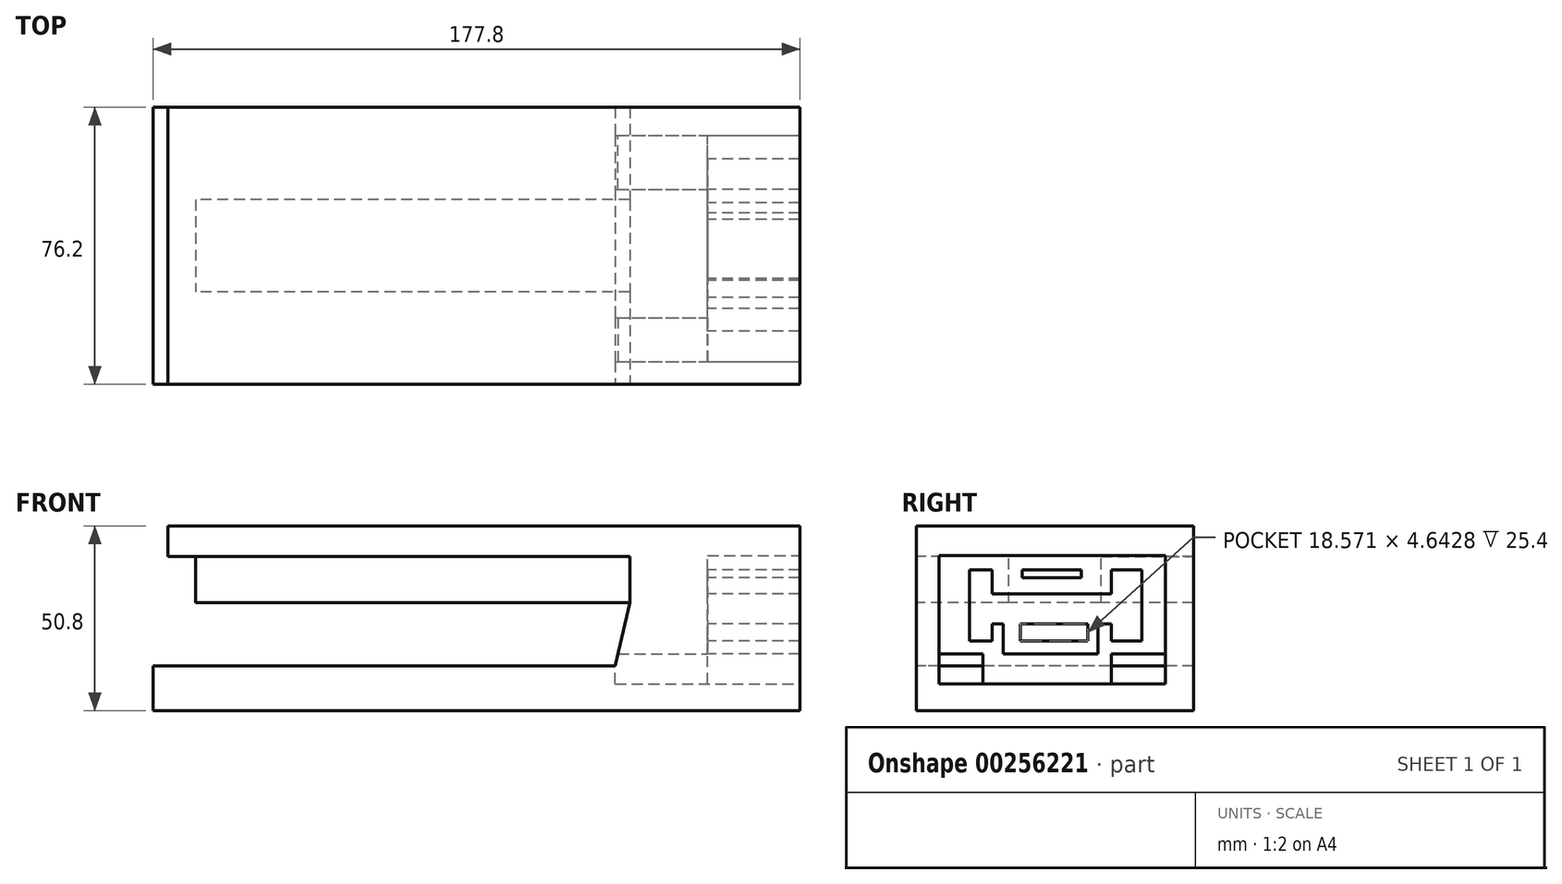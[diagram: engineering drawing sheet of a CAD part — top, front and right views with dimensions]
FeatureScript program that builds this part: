
annotation { "Feature Type Name" : "Feature", "Feature Type Description" : "" }
export const myFeature = defineFeature(function(context is Context, id is Id, definition is map)
    precondition{}
    {
        {
            var Q0;
            Q0=qCreatedBy(makeId("Front.planeOp"),FACE);
            var sketch = newSketch(context, id + "F0", { "sketchPlane" : qUnion([Q0])});
            skLineSegment(sketch, "E0", {"start": v(-114.83, -15.63) * mm, "end": v(62.97, -15.63) * mm});
            skLineSegment(sketch, "E1", {"start": v(62.97, -15.63) * mm, "end": v(62.97, 35.17) * mm});
            skLineSegment(sketch, "E2", {"start": v(62.97, 35.17) * mm, "end": v(-114.83, 35.17) * mm});
            skLineSegment(sketch, "E3", {"start": v(-114.83, 35.17) * mm, "end": v(-114.83, -15.63) * mm});
            skSolve(sketch);
        }
        {
            var Q0;
            Q0=makeQuery(id+"F0.imprint","IMPRINT",FACE,{"disambiguationData":[TD([[makeQuery(id+"F0.imprint","IMPRINT",EDGE,{"derivedFrom":sQuery(id+"F0.wireOp",EDGE,"E0")}),1.0]])]});
            extrude(context, id + "F1", {"entities" : qUnion([Q0]), "depth" : 76.2 * mm});
        }
        {
            var Q0;
            Q0=makeQuery(id+"F1.opExtrude","CAP_FACE",FACE,{"disambiguationData":[OSD([sQuery(id+"F0.wireOp",EDGE,"E0"),sQuery(id+"F0.wireOp",EDGE,"E1"),sQuery(id+"F0.wireOp",EDGE,"E2"),sQuery(id+"F0.wireOp",EDGE,"E3")])],"isStart":false});
            var sketch = newSketch(context, id + "F2", { "sketchPlane" : qUnion([Q0])});
            skLineSegment(sketch, "E4", {"start": v(-114.83, -3.25) * mm, "end": v(12.17, -3.25) * mm});
            skLineSegment(sketch, "E5", {"start": v(12.17, -3.25) * mm, "end": v(16.2, 14.07) * mm});
            skLineSegment(sketch, "E6", {"start": v(16.2, 14.07) * mm, "end": v(-103.19, 14.07) * mm});
            skLineSegment(sketch, "E7", {"start": v(-103.19, 14.07) * mm, "end": v(-103.19, 26.77) * mm});
            skLineSegment(sketch, "E8", {"start": v(-103.19, 26.77) * mm, "end": v(-110.8, 26.77) * mm});
            skLineSegment(sketch, "E9", {"start": v(-110.8, 26.77) * mm, "end": v(-110.8, 35.17) * mm});
            skLineSegment(sketch, "E10", {"start": v(-110.8, 35.17) * mm, "end": v(-114.83, 35.17) * mm});
            skLineSegment(sketch, "E11", {"start": v(-114.83, 35.17) * mm, "end": v(-114.83, -3.25) * mm});
            skSolve(sketch);
        }
        {
            var Q0;
            Q0=makeQuery(id+"F2.imprint","IMPRINT",FACE,{"disambiguationData":[TD([[makeQuery(id+"F2.imprint","IMPRINT",EDGE,{"derivedFrom":sQuery(id+"F2.wireOp",EDGE,"E4")}),1.0]])]});
            extrude(context, id + "F3", {"entities" : qUnion([Q0]), "operationType" : NewBodyOperationType.REMOVE, "oppositeDirection" : true, "depth" : 76.2 * mm});
        }
        {
            var Q0;
            Q0=makeQuery(id+"F1.opExtrude","CAP_FACE",FACE,{"disambiguationData":[OSD([sQuery(id+"F0.wireOp",EDGE,"E0"),sQuery(id+"F0.wireOp",EDGE,"E1"),sQuery(id+"F0.wireOp",EDGE,"E2"),sQuery(id+"F0.wireOp",EDGE,"E3")])],"isStart":false});
            var sketch = newSketch(context, id + "F4", { "sketchPlane" : qUnion([Q0])});
            skLineSegment(sketch, "E12", {"start": v(-103.19, 26.77) * mm, "end": v(16.2, 26.77) * mm});
            skLineSegment(sketch, "E13", {"start": v(16.2, 26.77) * mm, "end": v(16.2, 14.07) * mm});
            skLineSegment(sketch, "E14", {"start": v(16.2, 14.07) * mm, "end": v(-103.19, 14.07) * mm});
            skLineSegment(sketch, "E15", {"start": v(-103.19, 14.07) * mm, "end": v(-103.19, 26.77) * mm});
            skSolve(sketch);
        }
        {
            var Q0;
            Q0=makeQuery(id+"F4.imprint","IMPRINT",FACE,{"disambiguationData":[TD([[makeQuery(id+"F4.imprint","IMPRINT",EDGE,{"derivedFrom":sQuery(id+"F4.wireOp",EDGE,"E12")}),-1.0]])]});
            extrude(context, id + "F5", {"entities" : qUnion([Q0]), "operationType" : NewBodyOperationType.REMOVE, "oppositeDirection" : true, "depth" : 25.4 * mm});
        }
        {
            var Q0;
            Q0=makeQuery(id+"F1.opExtrude","CAP_FACE",FACE,{"disambiguationData":[OSD([sQuery(id+"F0.wireOp",EDGE,"E0"),sQuery(id+"F0.wireOp",EDGE,"E1"),sQuery(id+"F0.wireOp",EDGE,"E2"),sQuery(id+"F0.wireOp",EDGE,"E3")])],"isStart":true});
            var sketch = newSketch(context, id + "F6", { "sketchPlane" : qUnion([Q0])});
            skLineSegment(sketch, "E16", {"start": v(103.19, 26.77) * mm, "end": v(-16.2, 26.77) * mm});
            skLineSegment(sketch, "E17", {"start": v(-16.2, 26.77) * mm, "end": v(-16.2, 14.07) * mm});
            skLineSegment(sketch, "E18", {"start": v(-16.2, 14.07) * mm, "end": v(103.19, 14.07) * mm});
            skLineSegment(sketch, "E19", {"start": v(103.19, 14.07) * mm, "end": v(103.19, 26.77) * mm});
            skSolve(sketch);
        }
        {
            var Q0;
            Q0=makeQuery(id+"F6.imprint","IMPRINT",FACE,{"disambiguationData":[TD([[makeQuery(id+"F6.imprint","IMPRINT",EDGE,{"derivedFrom":sQuery(id+"F6.wireOp",EDGE,"E16")}),1.0]])]});
            extrude(context, id + "F7", {"entities" : qUnion([Q0]), "operationType" : NewBodyOperationType.REMOVE, "oppositeDirection" : true, "depth" : 25.4 * mm});
        }
        {
            var Q0;
            Q0=makeQuery(id+"F1.opExtrude","SWEPT_FACE",FACE,{"disambiguationData":[OSD([sQuery(id+"F0.wireOp",EDGE,"E1")])]});
            var sketch = newSketch(context, id + "F8", { "sketchPlane" : qUnion([Q0])});
            skLineSegment(sketch, "E20.bottom", {"start": v(-69.95, -8.2) * mm, "end": v(-7.74, -8.2) * mm});
            skLineSegment(sketch, "E20.top", {"start": v(-69.95, 27.08) * mm, "end": v(-7.74, 27.08) * mm});
            skLineSegment(sketch, "E20.left", {"start": v(-69.95, -8.2) * mm, "end": v(-69.95, 27.08) * mm});
            skLineSegment(sketch, "E20.right", {"start": v(-7.74, -8.2) * mm, "end": v(-7.74, 27.08) * mm});
            skSolve(sketch);
        }
        {
            var Q0;
            Q0=makeQuery(id+"F8.imprint","IMPRINT",FACE,{"disambiguationData":[TD([[makeQuery(id+"F8.imprint","IMPRINT",EDGE,{"derivedFrom":sQuery(id+"F8.wireOp",EDGE,"E20.bottom")}),1.0]])]});
            extrude(context, id + "F9", {"entities" : qUnion([Q0]), "operationType" : NewBodyOperationType.REMOVE, "oppositeDirection" : true, "depth" : 25.4 * mm});
        }
        {
            var Q0;
            Q0=makeQuery(id+"F9.boolean.opBoolean","COPY",FACE,{"derivedFrom":makeQuery(id+"F9.opExtrude","CAP_FACE",FACE,{"disambiguationData":[OSD([sQuery(id+"F8.wireOp",EDGE,"E20.bottom"),sQuery(id+"F8.wireOp",EDGE,"E20.top"),sQuery(id+"F8.wireOp",EDGE,"E20.left"),sQuery(id+"F8.wireOp",EDGE,"E20.right")])],"isStart":false})});
            var sketch = newSketch(context, id + "F10", { "sketchPlane" : qUnion([Q0])});
            skLineSegment(sketch, "E21", {"start": v(-57.88, -8.2) * mm, "end": v(-57.88, 0) * mm});
            skLineSegment(sketch, "E22", {"start": v(-22.6, -8.2) * mm, "end": v(-22.6, 0) * mm});
            skLineSegment(sketch, "E23", {"start": v(-22.6, 0) * mm, "end": v(-7.74, 0) * mm});
            skLineSegment(sketch, "E24", {"start": v(-7.74, 0) * mm, "end": v(-7.74, -8.2) * mm});
            skLineSegment(sketch, "E25", {"start": v(-7.74, -8.2) * mm, "end": v(-22.6, -8.2) * mm});
            skLineSegment(sketch, "E26", {"start": v(-57.88, -8.2) * mm, "end": v(-69.95, -8.2) * mm});
            skLineSegment(sketch, "E27", {"start": v(-57.88, 0) * mm, "end": v(-69.95, 0) * mm});
            skLineSegment(sketch, "E28", {"start": v(-69.95, 0) * mm, "end": v(-69.95, -8.2) * mm});
            skSolve(sketch);
        }
        {
            var Q0;
            Q0=makeQuery(id+"F10.imprint","IMPRINT",FACE,{"disambiguationData":[TD([[makeQuery(id+"F10.imprint","IMPRINT",EDGE,{"derivedFrom":sQuery(id+"F10.wireOp",EDGE,"E21")}),1.0]])]});
            var Q1;
            Q1=makeQuery(id+"F10.imprint","IMPRINT",FACE,{"disambiguationData":[TD([[makeQuery(id+"F10.imprint","IMPRINT",EDGE,{"derivedFrom":sQuery(id+"F10.wireOp",EDGE,"E22")}),-1.0]])]});
            extrude(context, id + "F11", {"entities" : qUnion([Q0, Q1]), "operationType" : NewBodyOperationType.REMOVE, "oppositeDirection" : true, "depth" : 25.4 * mm});
        }
        {
            var Q0;
            Q0=makeQuery(id+"F9.boolean.opBoolean","COPY",FACE,{"derivedFrom":makeQuery(id+"F9.opExtrude","CAP_FACE",FACE,{"disambiguationData":[OSD([sQuery(id+"F8.wireOp",EDGE,"E20.bottom"),sQuery(id+"F8.wireOp",EDGE,"E20.top"),sQuery(id+"F8.wireOp",EDGE,"E20.left"),sQuery(id+"F8.wireOp",EDGE,"E20.right")])],"isStart":false})});
            var sketch = newSketch(context, id + "F12", { "sketchPlane" : qUnion([Q0])});
            skLineSegment(sketch, "E29", {"start": v(-61.6, 23.06) * mm, "end": v(-61.6, 3.56) * mm});
            skLineSegment(sketch, "E30", {"start": v(-61.6, 3.56) * mm, "end": v(-55.4, 3.56) * mm});
            skLineSegment(sketch, "E31", {"start": v(-55.4, 3.56) * mm, "end": v(-55.4, 8.2) * mm});
            skLineSegment(sketch, "E32", {"start": v(-55.4, 8.2) * mm, "end": v(-52.3, 8.2) * mm});
            skLineSegment(sketch, "E33", {"start": v(-52.3, 8.2) * mm, "end": v(-52.3, 16.56) * mm});
            skLineSegment(sketch, "E34", {"start": v(-52.3, 16.56) * mm, "end": v(-55.4, 16.56) * mm});
            skLineSegment(sketch, "E35", {"start": v(-55.4, 16.56) * mm, "end": v(-55.4, 23.06) * mm});
            skLineSegment(sketch, "E36", {"start": v(-55.4, 23.06) * mm, "end": v(-61.6, 23.06) * mm});
            skLineSegment(sketch, "E37", {"start": v(-14.24, 23.06) * mm, "end": v(-22.6, 23.06) * mm});
            skLineSegment(sketch, "E38", {"start": v(-22.6, 23.06) * mm, "end": v(-22.6, 16.56) * mm});
            skLineSegment(sketch, "E39", {"start": v(-22.6, 16.56) * mm, "end": v(-26.3, 16.56) * mm});
            skLineSegment(sketch, "E40", {"start": v(-26.3, 16.56) * mm, "end": v(-26.3, 8.2) * mm});
            skLineSegment(sketch, "E41", {"start": v(-26.3, 8.2) * mm, "end": v(-22.6, 8.2) * mm});
            skLineSegment(sketch, "E42", {"start": v(-22.6, 8.2) * mm, "end": v(-22.6, 3.56) * mm});
            skLineSegment(sketch, "E43", {"start": v(-22.6, 3.56) * mm, "end": v(-14.24, 3.56) * mm});
            skLineSegment(sketch, "E44", {"start": v(-14.24, 3.56) * mm, "end": v(-14.24, 23.06) * mm});
            skLineSegment(sketch, "E45", {"start": v(-52.3, 16.56) * mm, "end": v(-26.3, 16.56) * mm});
            skLineSegment(sketch, "E46", {"start": v(-26.3, 8.2) * mm, "end": v(-52.3, 8.2) * mm});
            skLineSegment(sketch, "E47", {"start": v(-52.3, 8.2) * mm, "end": v(-52.3, 0) * mm});
            skLineSegment(sketch, "E48", {"start": v(-52.3, 0) * mm, "end": v(-26.3, 0) * mm});
            skLineSegment(sketch, "E49", {"start": v(-26.3, 0) * mm, "end": v(-26.3, 8.2) * mm});
            skLineSegment(sketch, "E50", {"start": v(-29.1, 8.2) * mm, "end": v(-29.1, 3.56) * mm});
            skLineSegment(sketch, "E51", {"start": v(-29.1, 3.56) * mm, "end": v(-47.67, 3.56) * mm});
            skLineSegment(sketch, "E52", {"start": v(-47.67, 3.56) * mm, "end": v(-47.67, 8.2) * mm});
            skCircle(sketch, "E53", {"center": v(-39.3, 20.98) * mm, "radius": 2.08 * mm});
            skPoint(sketch, "E53.centerSnap0", {"position": v(-39.3, 16.56) * mm});
            skLineSegment(sketch, "E54.bottom", {"start": v(-47.17, 23.06) * mm, "end": v(-30.84, 23.06) * mm});
            skLineSegment(sketch, "E54.top", {"start": v(-47.17, 20.98) * mm, "end": v(-30.84, 20.98) * mm});
            skLineSegment(sketch, "E54.left", {"start": v(-47.17, 23.06) * mm, "end": v(-47.17, 20.98) * mm});
            skLineSegment(sketch, "E54.right", {"start": v(-30.84, 23.06) * mm, "end": v(-30.84, 20.98) * mm});
            skSolve(sketch);
        }
        {
            var Q0;
            Q0=makeQuery(id+"F12.imprint","IMPRINT",FACE,{"disambiguationData":[TD([[makeQuery(id+"F12.imprint","IMPRINT",EDGE,{"derivedFrom":sQuery(id+"F12.wireOp",EDGE,"E29")}),1.0]])]});
            var Q1;
            {var subQ3=sQuery(id+"F12.wireOp",EDGE,"E33");Q1=makeQuery(id+"F12.imprint","IMPRINT",FACE,{"disambiguationData":[TD([[makeQuery(id+"F12.imprint","IMPRINT",EDGE,{"derivedFrom":subQ3}),-1.0]])]});}
            var Q2;
            {var subQ0=sQuery(id+"F12.wireOp",EDGE,"E47");Q2=makeQuery(id+"F12.imprint","IMPRINT",FACE,{"disambiguationData":[TD([[makeQuery(id+"F12.imprint","IMPRINT",EDGE,{"derivedFrom":subQ0}),1.0]])]});}
            var Q3;
            {var subQ0=sQuery(id+"F12.wireOp",EDGE,"E54.top");var subQ1=sQuery(id+"F12.wireOp",EDGE,"E53");var subQ2=makeQuery(id+"F12.imprint","INTERSECT",VERTEX,{"disambiguationData":[OD(0.0)],"derivedFrom":[subQ1,subQ0]});Q3=makeQuery(id+"F12.imprint","IMPRINT",FACE,{"disambiguationData":[TD([[makeQuery(id+"F12.imprint","IMPRINT",EDGE,{"disambiguationData":[TD([[subQ2,1.0]])],"derivedFrom":subQ1}),1.0]])]});}
            var Q4;
            {var subQ0=sQuery(id+"F12.wireOp",EDGE,"E53");var subQ1=makeQuery(id+"F12.imprint","INTERSECT",VERTEX,{"derivedFrom":[subQ0,sQuery(id+"F12.wireOp",EDGE,"E54.bottom")]});Q4=makeQuery(id+"F12.imprint","IMPRINT",FACE,{"disambiguationData":[TD([[makeQuery(id+"F12.imprint","IMPRINT",EDGE,{"disambiguationData":[TD([[subQ1,1.0]])],"derivedFrom":subQ0}),1.0]])]});}
            var Q5;
            {var subQ5=sQuery(id+"F12.wireOp",EDGE,"E54.left");Q5=makeQuery(id+"F12.imprint","IMPRINT",FACE,{"disambiguationData":[TD([[makeQuery(id+"F12.imprint","IMPRINT",EDGE,{"derivedFrom":subQ5}),1.0]])]});}
            var Q6;
            {var subQ5=sQuery(id+"F12.wireOp",EDGE,"E54.right");Q6=makeQuery(id+"F12.imprint","IMPRINT",FACE,{"disambiguationData":[TD([[makeQuery(id+"F12.imprint","IMPRINT",EDGE,{"derivedFrom":subQ5}),-1.0]])]});}
            var Q7;
            Q7=makeQuery(id+"F12.imprint","IMPRINT",FACE,{"disambiguationData":[TD([[makeQuery(id+"F12.imprint","IMPRINT",EDGE,{"derivedFrom":sQuery(id+"F12.wireOp",EDGE,"E37")}),1.0]])]});
            extrude(context, id + "F13", {"entities" : qUnion([Q0, Q1, Q2, Q3, Q4, Q5, Q6, Q7]), "operationType" : NewBodyOperationType.ADD, "depth" : 25.4 * mm});
        }
    });
